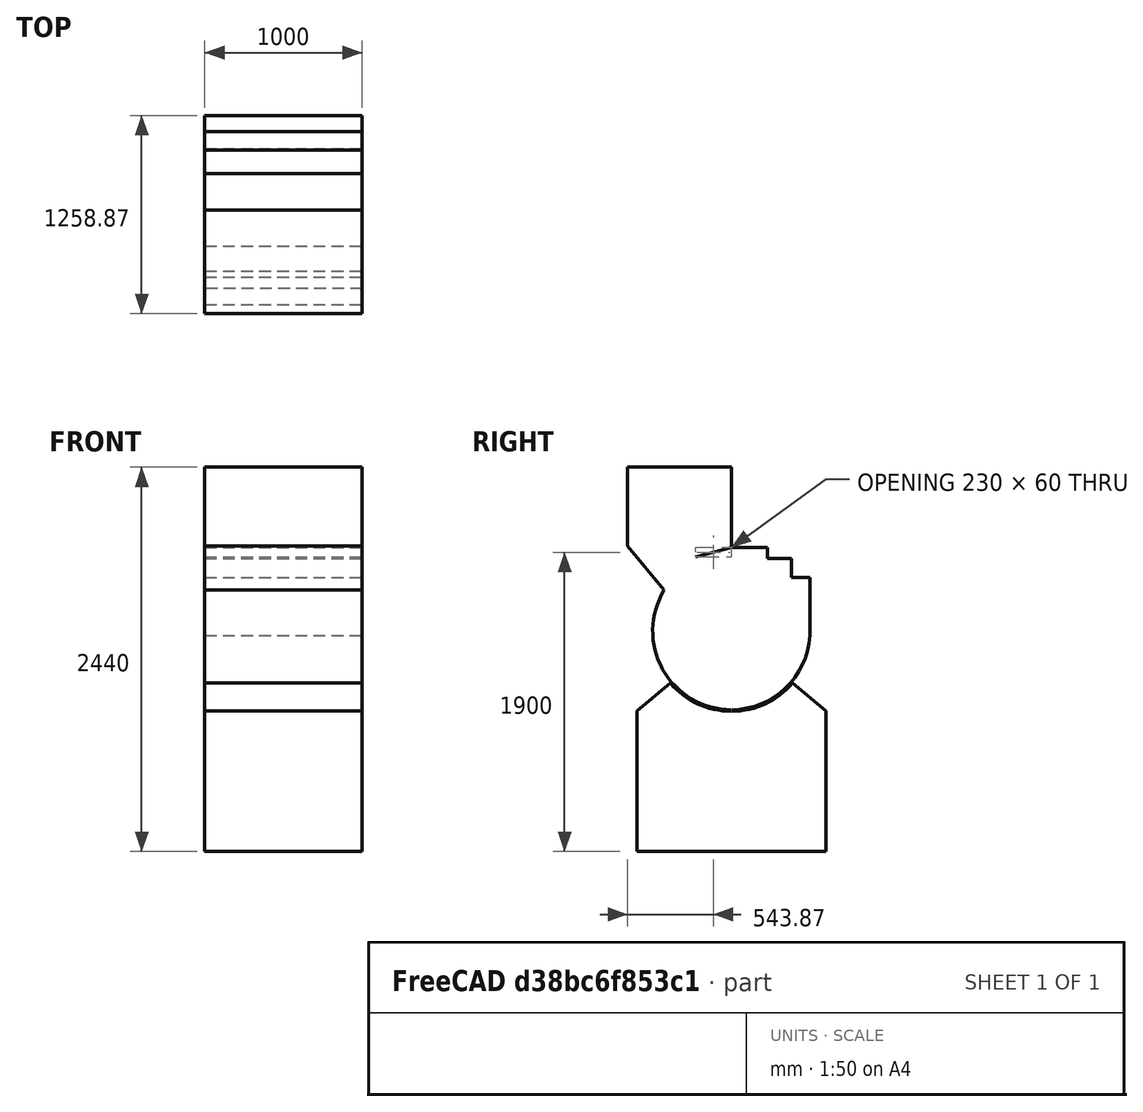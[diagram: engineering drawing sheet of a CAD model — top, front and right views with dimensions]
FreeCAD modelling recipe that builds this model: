
FCSTD DOCUMENT
Label: Shell
objects: Sketcher::SketchObject×1, PartDesign::Pad×1
note: 3 computed .brp shape members not serialized (recipe doc carries the construction recipe); baked Part::Feature solids carry a one-line shape summary decoded from their .brp

FEATURE [Sketcher::SketchObject] Sketch  label="Shell "
  Placement = pos=(-500,0,0) rot=(0.57735,0.57735,0.57735;2.0944rad)
  sketch-geometry (22):
    g0: ArcOfCircle CenterX=0 CenterY=0 CenterZ=0 NormalX=0 NormalY=0 NormalZ=1 Radius=500 StartAngle=2.59474 EndAngle=4.70765
    g1: LineSegment StartX=-427.083 StartY=260 StartZ=0 EndX=-658.874 EndY=540 EndZ=0
    g2: LineSegment StartX=0 StartY=530 StartZ=0 EndX=230 EndY=530 EndZ=0
    g3: LineSegment StartX=230 StartY=530 StartZ=0 EndX=230 EndY=460 EndZ=0
    g4: LineSegment StartX=230 StartY=460 StartZ=0 EndX=380 EndY=460 EndZ=0
    g5: LineSegment StartX=380 StartY=460 StartZ=0 EndX=380 EndY=340 EndZ=0
    g6: LineSegment StartX=380 StartY=340 StartZ=0 EndX=499.099 EndY=340 EndZ=0
    g7: LineSegment StartX=499.099 StartY=340 StartZ=0 EndX=499.099 EndY=-30 EndZ=0
    g8: LineSegment StartX=-658.874 StartY=1040 StartZ=0 EndX=-658.874 EndY=540 EndZ=0
    g9: LineSegment StartX=0 StartY=530 StartZ=0 EndX=-230 EndY=470 EndZ=0
    g10: LineSegment StartX=-388.591 StartY=-330.298 StartZ=0 EndX=-600 EndY=-507.691 EndZ=0
    g11: LineSegment StartX=-600 StartY=-507.691 StartZ=0 EndX=-600 EndY=-1400 EndZ=0
    g12: LineSegment StartX=-600 StartY=-1400 StartZ=0 EndX=600 EndY=-1400 EndZ=0
    g13: LineSegment StartX=600 StartY=-1400 StartZ=0 EndX=600 EndY=-507.691 EndZ=0
    g14: LineSegment StartX=600 StartY=-507.691 StartZ=0 EndX=388.591 EndY=-330.298 EndZ=0
    g15: ArcOfCircle CenterX=0 CenterY=0 CenterZ=0 NormalX=0 NormalY=0 NormalZ=1 Radius=510 StartAngle=3.84608 EndAngle=4.70774
    g16: LineSegment StartX=-2.36852 StartY=-499.994 StartZ=0 EndX=-2.36852 EndY=-509.995 EndZ=0
    g17: LineSegment StartX=2.36852 StartY=-499.994 StartZ=0 EndX=2.36852 EndY=-509.995 EndZ=0
    g18: ArcOfCircle CenterX=0 CenterY=0 CenterZ=0 NormalX=0 NormalY=0 NormalZ=1 Radius=500 StartAngle=4.71713 EndAngle=6.22315
    g19: ArcOfCircle CenterX=0 CenterY=0 CenterZ=0 NormalX=0 NormalY=0 NormalZ=1 Radius=510 StartAngle=4.71703 EndAngle=5.5787
    g20: LineSegment StartX=-658.874 StartY=1040 StartZ=0 EndX=0 EndY=1040 EndZ=0
    g21: LineSegment StartX=0 StartY=1040 StartZ=0 EndX=0 EndY=530 EndZ=0
  constraints (68):
    c: Radius(g0) = 500
    c: DistanceX(g0) = 0
    c: DistanceY(g0) = 0
    c: Horizontal(g2)
    c: Vertical(g3)
    c: Coincident(g4,g3)
    c: Horizontal(g4)
    c: Vertical(g5)
    c: Coincident(g6,g5)
    c: Horizontal(g6)
    c: DistanceY(g1) = 540
    c: Coincident(g2,g3)
    c: Coincident(g4,g5)
    c: Coincident(g7,g18)
    c: Vertical(g7)
    c: Distance(g7) = 370
    c: Coincident(g1,g0)
    c: Coincident(g8,g1)
    c: Vertical(g8)
    c: Distance(g1) = 363.493
    c: Distance(g8) = 500
    c: Coincident(g11,g10)
    c: Vertical(g11)
    c: Horizontal(g12)
    c: Coincident(g13,g12)
    c: Vertical(g13)
    c: Coincident(g14,g13)
    c: Coincident(g12,g11)
    c: Equal(g13,g11)
    c: DistanceX(g12) = 600
    c: DistanceY(g12) = -1400
    c: Angle(g11,g10) = 2.26893
    c: Angle(g14,g13) = 2.26893
    c: Distance(g11) = 892.309
    c: Distance(g12) = 1200
    c: Radius(g15) = 510
    c: DistanceX(g15) = 0
    c: DistanceY(g15) = 0
    c: Coincident(g15,g10)
    c: Coincident(g14,g19)
    c: Vertical(g16)
    c: Equal(g17,g16)
    c: Equal(g0,g18)
    c: Coincident(g0,g16)
    c: Coincident(g18,g17)
    c: Coincident(g0,g18)
    c: Equal(g15,g19)
    c: Coincident(g15,g16)
    c: Coincident(g19,g17)
    c: Coincident(g15,g19)
    c: Vertical(g17)
    c: Distance(g16) = 10.0001
    c: Coincident(g20,g8)
    c: Horizontal(g20)
    c: Coincident(g21,g20)
    c: Vertical(g21)
    c: Coincident(g6,g7)
    c: Coincident(g9,g2)
    c: Coincident(g21,g2)
    c: DistanceX(g5) = 380
    c: DistanceY(g5) = 340
    c: DistanceX(g3) = 230
    c: DistanceY(g3) = 460
    c: DistanceX(g2) = 0
    c: DistanceY(g2) = 530
    c: DistanceX(g9) = -230
    c: DistanceY(g9) = 470
    c: DistanceY(g0) = 260
FEATURE [PartDesign::Pad] Pad  label="Shell_"
  Length = 1000
  MirroredExtent = false
  Sketch = -> Sketch
